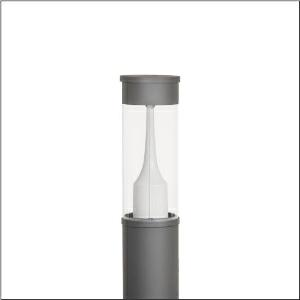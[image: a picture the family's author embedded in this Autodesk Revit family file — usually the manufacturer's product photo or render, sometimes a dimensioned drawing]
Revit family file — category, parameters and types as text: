
# Revit family: city-light_120_iq___pl1_2s_5xa5285of14h_ee05
name_source: partatom
category: Lighting Fixtures
units: mm (PartAtom-declared; Revit-internal decimal feet)

## family parameters
Cut with Voids When Loaded = No
Host = Face
Light Source = No
Part Type = Normal
Room Calculation Point = No
Round Connector Dimension = Use Diameter
Shared = No

## types (1)
- --- (1 x LED, 2970 lm, 21.8 W, 2700K)
    Apparent Load = 22 VA
    CIE Flux Codes = 23 62 94 96 100
    Color Rendering = 70
    Color Temperature = 2700K
    Default Elevation = 1800 mm
    Description = City-Light 120 iQ, bollard luminaire, Module 540 iQ-SR, primary light control with 3 zone facetted reflector, of plastic, silver coated, highly specular, structured, primary optical cover: cover, of PMMA, transparent, partly coated, light distribution: PL1.2s, primary light characteristic: symmetric, LED, High Power LED, rated luminous flux: 2.970lm, luminous efficacy: 136lm/W, light colour: 727, colour temperature: 2700K, control gear: ECG iQ, control: presetting dimming logarithmic, Street-Remote, Auto-Match, Temp-Guard, Lumen-Switch, Night-Set, Smart-Wire, Light-Fading, Desk-Remote (wireless, voltage-free reading and setting of iQ features in the workshop via application-optimized NFC function/RFID function), optimised constant luminous flux control (CLO 2.0), with terminal, 6-pole, max. 2.5mm², mains connection: 230..240V, AC, 50/60Hz, start of lifetime: 22W, end of service life: 23W, reduction: 11W, luminaire housing, cylindrical, of extruded aluminium section, coated, Siteco® metallic grey (DB 702S), length: 1.200mm, diameter: 200mm, Module 540 iQ-SR, traffic white (RAL 9016), equipment: standard, protection rating (complete): IP54, insulation class (complete): insulation class II (safety insulation), certification: CE, ENEC, VDE, packaging unit: 1 piece

Light Distribution: PL1.2s
    Height = 500 mm
    Lamp = 1 x LED
    Lamp Light Flux = 2970 lm
    Lamp Power = 21.8 W
    Lamp count = 1
    Length = 200 mm  [stored 0.656168 ft]
    Luminous efficacy = 136 lm/W
    Manufacturer = Siteco
    ModVariant = No
    Model = 5XA5285OF14H
    Mounting Place = Floor
    Mounting Type = Freestanding
    Number of Poles = 1
    OnlyDefault = Yes
    Power Factor = 1
    Product Name = City-Light 120 iQ | PL1.2s
    Product group = bollard luminaire
    ProductGroupID = 1304
    Protection Class = Protection class II
    Protection Degree = IP 54
    RLX_Detail_Level = 1
    RLX_Emergency_Light_Flux = 0 lm
    RLX_Emergency_Type = 0
    RLX_Emergency_Type_DB = No
    RlxData = <blob elided: 30197 chars, md5=9325beba>
    Socket = socket
    Standby Power = 0 W
    System Light Flux = 2970 lm
    System Power = 22 W
    Type Comments = factory setting: luminous flux: 100 % | dim-lin: 254 | 456 mA
    Type Image = l_1006922.jpg
    URL = http://relux.com
    VarID = @adj_094689
    Voltage = 0 V
    Weight = 0.00 kg
    Width = 0 mm  [stored 0 ft]

note: [stored X ft] marks values corroborated as IEEE doubles in the binary element streams (Revit-internal decimal feet)

## geometry (parser evidence)
native form markers: Blend x4, Sweep x10
no freeform markers — native parametric forms only
